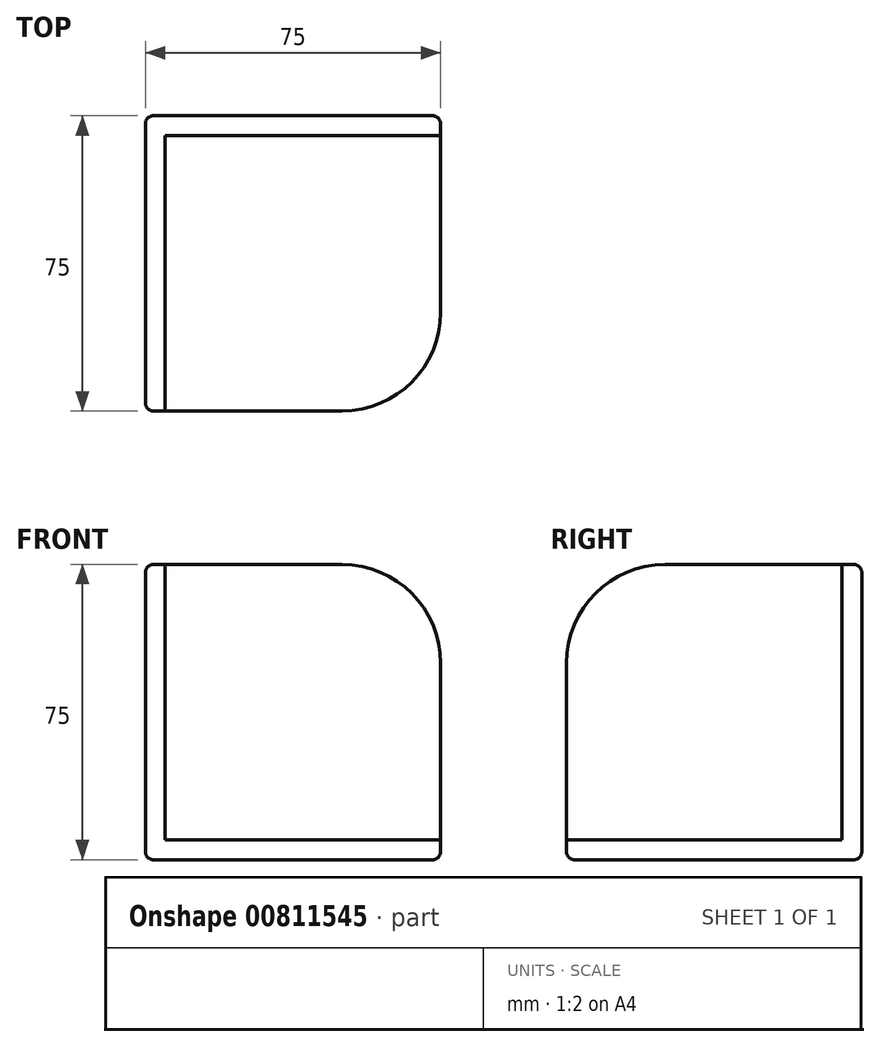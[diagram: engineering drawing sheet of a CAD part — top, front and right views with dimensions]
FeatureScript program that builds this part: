
annotation { "Feature Type Name" : "Feature", "Feature Type Description" : "" }
export const myFeature = defineFeature(function(context is Context, id is Id, definition is map)
    precondition{}
    {
        {
            var Q0;
            Q0=qCreatedBy(makeId("Top.planeOp"),FACE);
            var sketch = newSketch(context, id + "F0", { "sketchPlane" : qUnion([Q0])});
            skLineSegment(sketch, "E0.bottom", {"start": v(37.5, -37.5) * mm, "end": v(-37.5, -37.5) * mm});
            skLineSegment(sketch, "E0.top", {"start": v(37.5, 37.5) * mm, "end": v(-37.5, 37.5) * mm});
            skLineSegment(sketch, "E0.left", {"start": v(37.5, -37.5) * mm, "end": v(37.5, 37.5) * mm});
            skLineSegment(sketch, "E0.right", {"start": v(-37.5, -37.5) * mm, "end": v(-37.5, 37.5) * mm});
            skPoint(sketch, "E0.middle", {"position": v(0, 0) * mm});
            skSolve(sketch);
        }
        {
            var Q0;
            Q0=makeQuery(id+"F0.imprint","IMPRINT",FACE,{"disambiguationData":[TD([[makeQuery(id+"F0.imprint","IMPRINT",EDGE,{"derivedFrom":sQuery(id+"F0.wireOp",EDGE,"E0.bottom")}),-1.0]])]});
            extrude(context, id + "F1", {"entities" : qUnion([Q0]), "depth" : 5 * mm, "offsetDistance" : 25 * mm});
        }
        {
            var Q0;
            Q0=makeQuery(id+"F1.opExtrude","CAP_FACE",FACE,{"disambiguationData":[OSD([sQuery(id+"F0.wireOp",EDGE,"E0.bottom"),sQuery(id+"F0.wireOp",EDGE,"E0.top"),sQuery(id+"F0.wireOp",EDGE,"E0.left"),sQuery(id+"F0.wireOp",EDGE,"E0.right")])],"isStart":false});
            var sketch = newSketch(context, id + "F2", { "sketchPlane" : qUnion([Q0])});
            skLineSegment(sketch, "E1.bottom", {"start": v(-37.5, 37.5) * mm, "end": v(-32.5, 37.5) * mm});
            skLineSegment(sketch, "E1.top", {"start": v(-37.5, -37.5) * mm, "end": v(-32.5, -37.5) * mm});
            skLineSegment(sketch, "E1.left", {"start": v(-37.5, 37.5) * mm, "end": v(-37.5, -37.5) * mm});
            skLineSegment(sketch, "E1.right", {"start": v(-32.5, 37.5) * mm, "end": v(-32.5, -37.5) * mm});
            skLineSegment(sketch, "E2.bottom", {"start": v(-32.5, 37.5) * mm, "end": v(37.5, 37.5) * mm});
            skLineSegment(sketch, "E2.top", {"start": v(-32.5, 32.5) * mm, "end": v(37.5, 32.5) * mm});
            skLineSegment(sketch, "E2.left", {"start": v(-32.5, 37.5) * mm, "end": v(-32.5, 32.5) * mm});
            skLineSegment(sketch, "E2.right", {"start": v(37.5, 37.5) * mm, "end": v(37.5, 32.5) * mm});
            skSolve(sketch);
        }
        {
            var Q0;
            Q0 = qSketchRegion(id + "F2", true);
            extrude(context, id + "F3", {"entities" : qUnion([Q0]), "operationType" : NewBodyOperationType.ADD, "depth" : 70 * mm, "offsetDistance" : 25 * mm});
        }
        {
            var Q0;
            Q0=makeQuery(id+"F3.opExtrude","CAP_EDGE",EDGE,{"disambiguationData":[OSD([sQuery(id+"F2.wireOp",EDGE,"E2.right")])],"isStart":false});
            var Q1;
            Q1=makeQuery(id+"F3.opExtrude","CAP_EDGE",EDGE,{"disambiguationData":[OSD([sQuery(id+"F2.wireOp",EDGE,"E1.top")])],"isStart":false});
            var Q2;
            Q2=makeQuery(id+"F1.opExtrude","SWEPT_EDGE",EDGE,{"disambiguationData":[OSD([sQuery(id+"F0.wireOp",EDGE,"E0.bottom"),sQuery(id+"F0.wireOp",EDGE,"E0.left")])]});
            fillet(context, id + "F4", {"entities" : qUnion([Q0, Q1, Q2]), "radius" : 25 * mm, "tangentPropagation" : true, "allowEdgeOverflow" : false});
        }
        {
            var Q0;
            Q0=makeQuery(id+"F1.opExtrude","CAP_FACE",FACE,{"disambiguationData":[OSD([sQuery(id+"F0.wireOp",EDGE,"E0.bottom"),sQuery(id+"F0.wireOp",EDGE,"E0.top"),sQuery(id+"F0.wireOp",EDGE,"E0.left"),sQuery(id+"F0.wireOp",EDGE,"E0.right")])],"isStart":true});
            var Q1;
            Q1=makeQuery(id+"F3.boolean.opBoolean","MERGE",FACE,{"derivedFrom":[makeQuery(id+"F1.opExtrude","SWEPT_FACE",FACE,{"disambiguationData":[OSD([sQuery(id+"F0.wireOp",EDGE,"E0.right")])]}),makeQuery(id+"F3.opExtrude","SWEPT_FACE",FACE,{"disambiguationData":[OSD([sQuery(id+"F2.wireOp",EDGE,"E1.left")])]})]});
            var Q2;
            Q2=makeQuery(id+"F3.boolean.opBoolean","MERGE",FACE,{"derivedFrom":[makeQuery(id+"F1.opExtrude","SWEPT_FACE",FACE,{"disambiguationData":[OSD([sQuery(id+"F0.wireOp",EDGE,"E0.top")])]}),makeQuery(id+"F3.opExtrude","SWEPT_FACE",FACE,{"disambiguationData":[OSD([sQuery(id+"F2.wireOp",EDGE,"E1.bottom"),sQuery(id+"F2.wireOp",EDGE,"E2.bottom")])]})]});
            fillet(context, id + "F5", {"entities" : qUnion([Q0, Q1, Q2]), "radius" : 2 * mm, "tangentPropagation" : true, "allowEdgeOverflow" : false});
        }
    });
